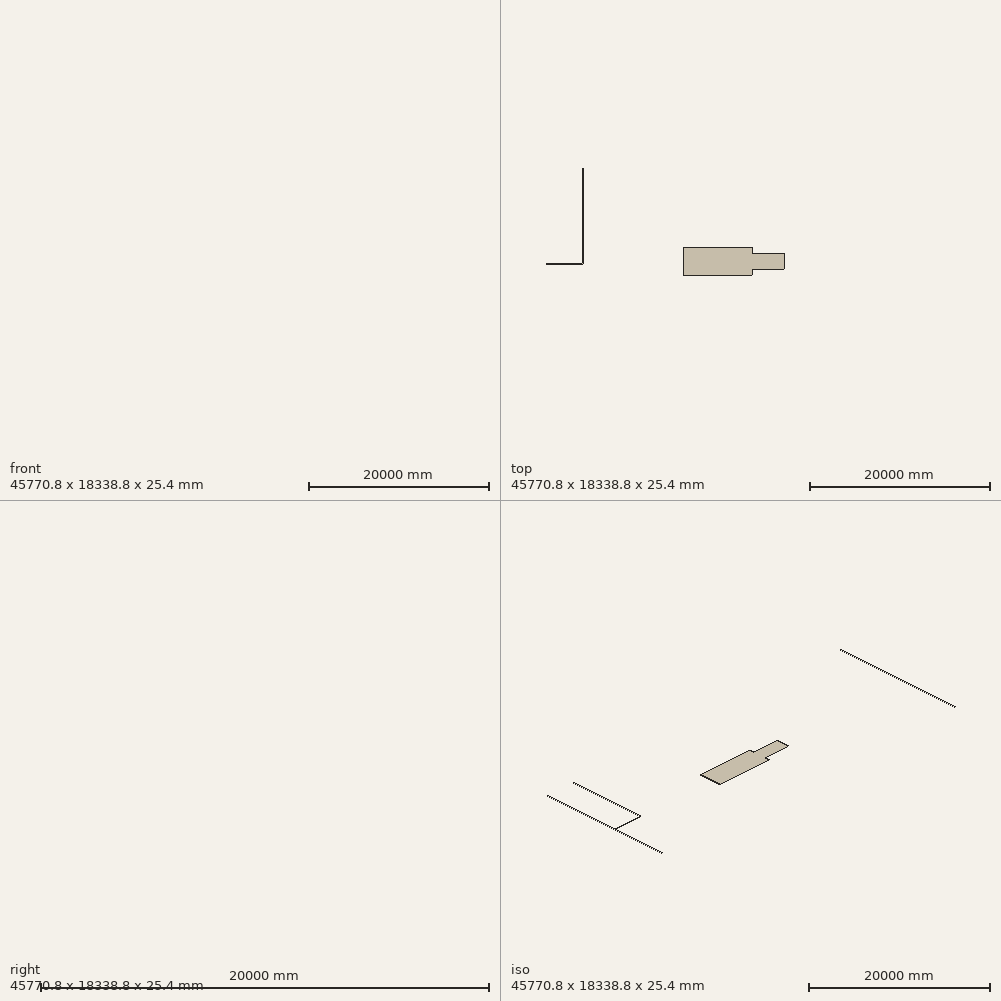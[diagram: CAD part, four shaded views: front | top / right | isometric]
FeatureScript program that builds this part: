
annotation { "Feature Type Name" : "Feature", "Feature Type Description" : "" }
export const myFeature = defineFeature(function(context is Context, id is Id, definition is map)
    precondition{}
    {
        {
            var Q0;
            Q0=qCreatedBy(makeId("Top.planeOp"),FACE);
            var sketch = newSketch(context, id + "F0", { "sketchPlane" : qUnion([Q0])});
            skLineSegment(sketch, "E0.bottom", {"start": v(0, 0) * mm, "end": v(7696.2, 0) * mm});
            skLineSegment(sketch, "E0.top", {"start": v(0, 3048) * mm, "end": v(7696.2, 3048) * mm});
            skLineSegment(sketch, "E0.left", {"start": v(0, 0) * mm, "end": v(0, 3048) * mm});
            skLineSegment(sketch, "E0.right", {"start": v(7696.2, 0) * mm, "end": v(7696.2, 3048) * mm});
            skLineSegment(sketch, "E1", {"start": v(7696.2, 2438.4) * mm, "end": v(11353.8, 2438.4) * mm});
            skLineSegment(sketch, "E2", {"start": v(11353.8, 2438.4) * mm, "end": v(11353.8, 609.6) * mm});
            skLineSegment(sketch, "E3", {"start": v(11353.8, 609.6) * mm, "end": v(7696.2, 609.6) * mm});
            skSolve(sketch);
        }
        {
            var Q0;
            {var subQ1=sQuery(id+"F0.wireOp",EDGE,"E0.bottom");Q0=makeQuery(id+"F0.imprint","IMPRINT",FACE,{"disambiguationData":[TD([[makeQuery(id+"F0.imprint","IMPRINT",EDGE,{"derivedFrom":subQ1}),1.0]])]});}
            var Q1;
            {var subQ0=sQuery(id+"F0.wireOp",EDGE,"E1");Q1=makeQuery(id+"F0.imprint","IMPRINT",FACE,{"disambiguationData":[TD([[makeQuery(id+"F0.imprint","IMPRINT",EDGE,{"derivedFrom":subQ0}),-1.0]])]});}
            extrude(context, id + "F1", {"entities" : qUnion([Q0, Q1]), "depth" : 25.4 * mm, "offsetDistance" : 25.4 * mm});
        }
        {
            var Q0;
            Q0=qCreatedBy(makeId("Top.planeOp"),FACE);
            var sketch = newSketch(context, id + "F2", { "sketchPlane" : qUnion([Q0])});
            skLineSegment(sketch, "E4", {"start": v(-15240, 11887.2) * mm, "end": v(-15240, -6400.8) * mm});
            skLineSegment(sketch, "E5", {"start": v(-15240, -6400.8) * mm, "end": v(30480, -6400.8) * mm});
            skLineSegment(sketch, "E6", {"start": v(30480, -6400.8) * mm, "end": v(30480, 11887.2) * mm});
            skLineSegment(sketch, "E7", {"start": v(30480, 11887.2) * mm, "end": v(-15240, 11887.2) * mm});
            skLineSegment(sketch, "E8", {"start": v(-11176, 11887.2) * mm, "end": v(-11176, 1219.2) * mm});
            skLineSegment(sketch, "E9", {"start": v(-11176, 1219.2) * mm, "end": v(-15240, 1219.2) * mm});
            skLineSegment(sketch, "E10.0", {"start": v(-11201.4, 11887.2) * mm, "end": v(-11201.4, 1219.2) * mm});
            skLineSegment(sketch, "E11.0", {"start": v(-11176, 1244.6) * mm, "end": v(-15240, 1244.6) * mm});
            skLineSegment(sketch, "E12.0", {"start": v(-15265.4, 11912.6) * mm, "end": v(-15265.4, -6426.2) * mm});
            skLineSegment(sketch, "E12.1", {"start": v(30505.4, 11912.6) * mm, "end": v(-15265.4, 11912.6) * mm});
            skLineSegment(sketch, "E12.2", {"start": v(30505.4, -6426.2) * mm, "end": v(30505.4, 11912.6) * mm});
            skLineSegment(sketch, "E12.3", {"start": v(-15265.4, -6426.2) * mm, "end": v(30505.4, -6426.2) * mm});
            skSolve(sketch);
        }
        {
            var Q0;
            {var subQ8=sQuery(id+"F2.wireOp",EDGE,"E5");Q0=makeQuery(id+"F2.imprint","IMPRINT",FACE,{"disambiguationData":[TD([[makeQuery(id+"F2.imprint","IMPRINT",EDGE,{"derivedFrom":subQ8}),-1.0]])]});}
            var Q1;
            {var subQ0=sQuery(id+"F2.wireOp",EDGE,"E8");var subQ1=sQuery(id+"F2.wireOp",EDGE,"E7");var subQ2=makeQuery(id+"F2.imprint","INTERSECT",VERTEX,{"derivedFrom":[subQ1,subQ0]});Q1=makeQuery(id+"F2.imprint","IMPRINT",FACE,{"disambiguationData":[TD([[makeQuery(id+"F2.imprint","IMPRINT",EDGE,{"disambiguationData":[TD([[subQ2,-1.0]])],"derivedFrom":subQ1}),1.0]])]});}
            var Q2;
            {var subQ0=sQuery(id+"F2.wireOp",EDGE,"E9");var subQ1=sQuery(id+"F2.wireOp",EDGE,"E4");var subQ2=makeQuery(id+"F2.imprint","INTERSECT",VERTEX,{"derivedFrom":[subQ1,subQ0]});Q2=makeQuery(id+"F2.imprint","IMPRINT",FACE,{"disambiguationData":[TD([[makeQuery(id+"F2.imprint","IMPRINT",EDGE,{"disambiguationData":[TD([[subQ2,1.0]])],"derivedFrom":subQ1}),1.0]])]});}
            var Q3;
            {var subQ0=sQuery(id+"F2.wireOp",EDGE,"E9");var subQ1=sQuery(id+"F2.wireOp",EDGE,"E8");var subQ2=makeQuery(id+"F2.imprint","INTERSECT",VERTEX,{"derivedFrom":[subQ1,subQ0]});Q3=makeQuery(id+"F2.imprint","IMPRINT",FACE,{"disambiguationData":[TD([[makeQuery(id+"F2.imprint","IMPRINT",EDGE,{"disambiguationData":[TD([[subQ2,1.0]])],"derivedFrom":subQ1}),-1.0]])]});}
            extrude(context, id + "F3", {"entities" : qUnion([Q0, Q1, Q2, Q3]), "depth" : 25.4 * mm, "offsetDistance" : 25.4 * mm});
        }
    });
